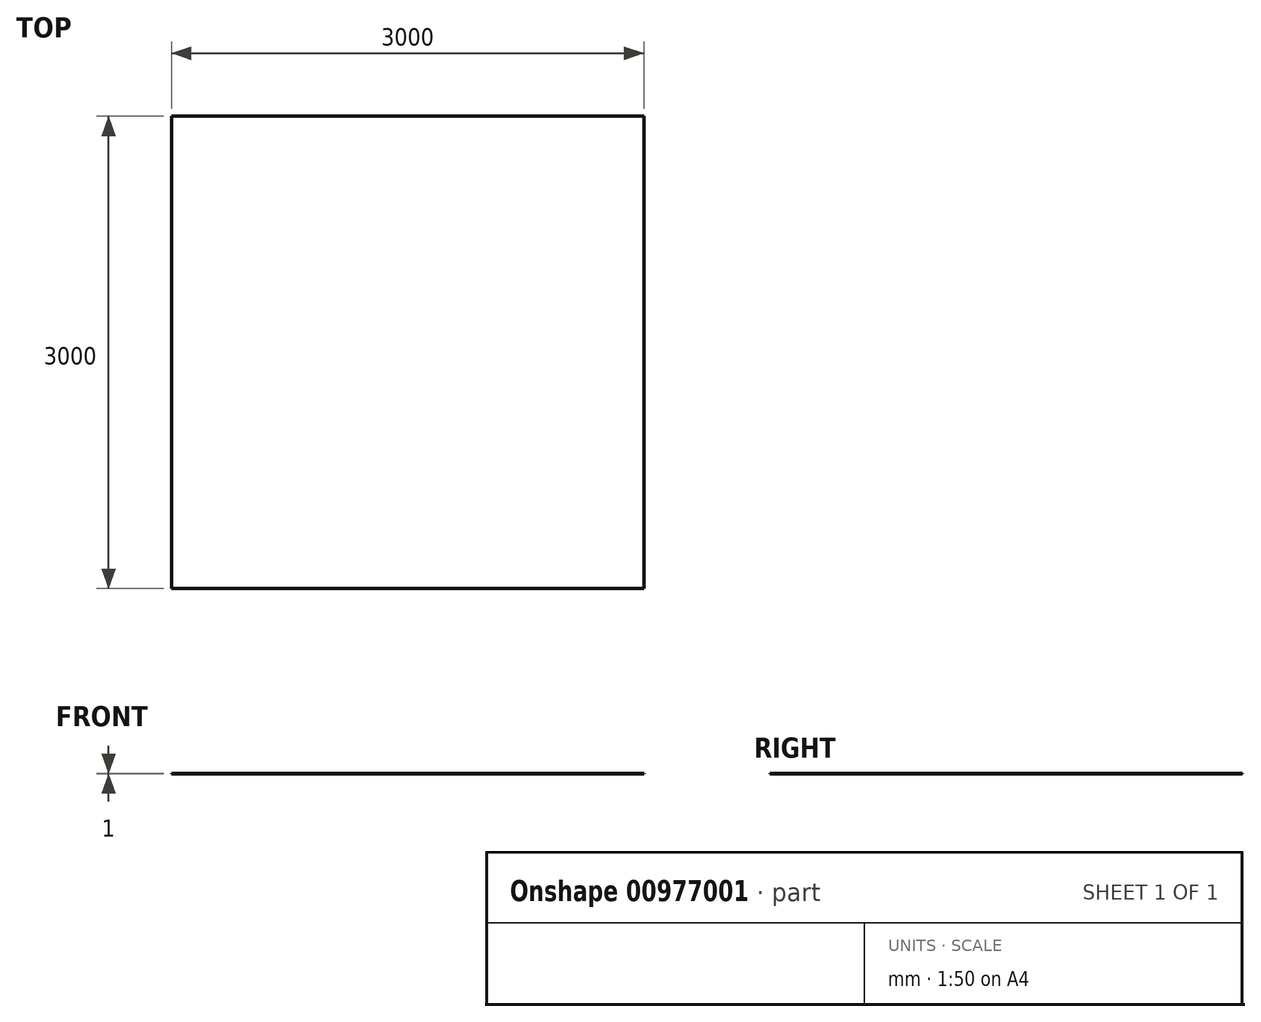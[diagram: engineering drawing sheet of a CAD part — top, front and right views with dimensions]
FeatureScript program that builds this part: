
annotation { "Feature Type Name" : "Feature", "Feature Type Description" : "" }
export const myFeature = defineFeature(function(context is Context, id is Id, definition is map)
    precondition{}
    {
        {
            var Q0;
            Q0=qCreatedBy(makeId("Top.planeOp"),FACE);
            var sketch = newSketch(context, id + "F0", { "sketchPlane" : qUnion([Q0])});
            skLineSegment(sketch, "E0.bottom", {"start": v(-1215.23, -1484.56) * mm, "end": v(1784.77, -1484.56) * mm});
            skLineSegment(sketch, "E0.top", {"start": v(-1215.23, 1515.44) * mm, "end": v(1784.77, 1515.44) * mm});
            skLineSegment(sketch, "E0.left", {"start": v(-1215.23, -1484.56) * mm, "end": v(-1215.23, 1515.44) * mm});
            skLineSegment(sketch, "E0.right", {"start": v(1784.77, -1484.56) * mm, "end": v(1784.77, 1515.44) * mm});
            skSolve(sketch);
        }
        {
            var Q0;
            Q0 = qSketchRegion(id + "F0", true);
            extrude(context, id + "F1", {"entities" : qUnion([Q0]), "oppositeDirection" : true, "depth" : 1 * mm, "offsetDistance" : 25 * mm});
        }
    });
